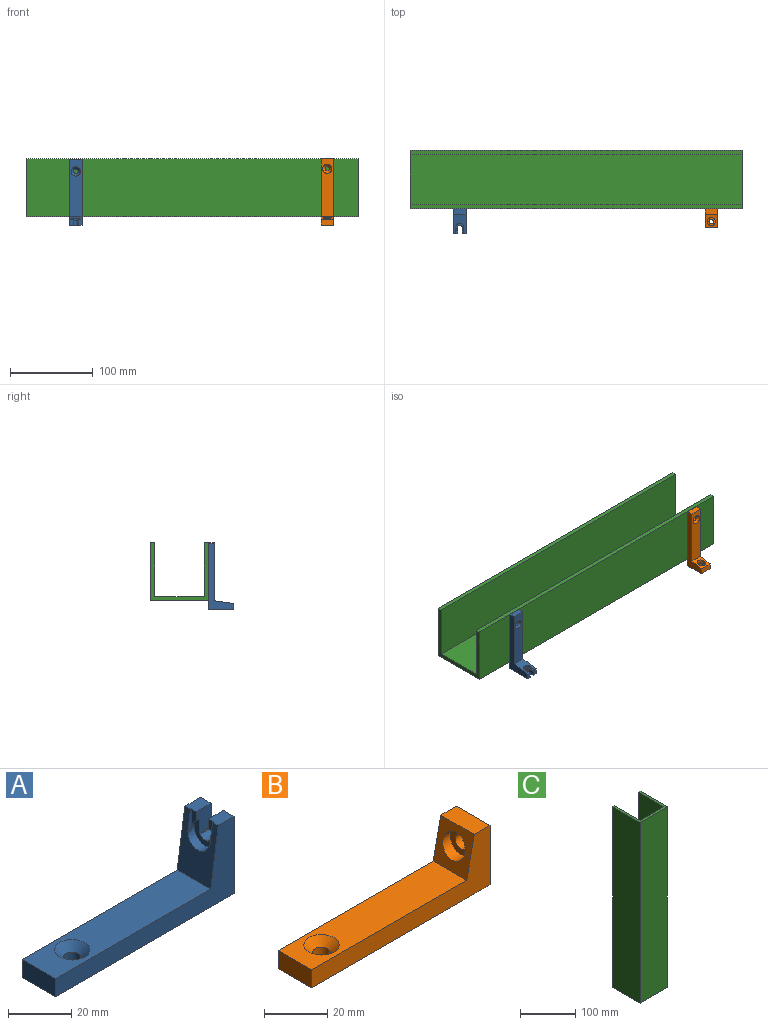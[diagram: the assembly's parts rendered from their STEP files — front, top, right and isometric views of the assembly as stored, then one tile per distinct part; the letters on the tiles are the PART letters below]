
ASSEMBLY  parts=3 mates=2
PART A: 24 faces, bbox 80x15x30 mm
  f0: cylinder r=4.88mm len=9.75mm, axis (-1,0,0), area 58.8mm2, adj f1,f2,f3,f7,f18,f19,f22,f23
  f1: plane 23x15mm, normal (-0.99,0,0.14), area 235.8mm2, adj f0,f4,f8,f9,f11,f15,f19,f20
  f2: plane 9x6.64mm, normal (0,-1,0), area 53mm2, adj f0,f5,f7,f15,f17,f23
  f3: plane 9x6.64mm, normal (0,1,0), area 53mm2, adj f0,f4,f5,f7,f16,f18
  f4: plane 7.07x4.75mm, normal (0,0,1), area 32.6mm2, adj f1,f3,f5,f11,f18,f20
  f5: plane 30x15mm, normal (1,0,0), area 396.4mm2, adj f2,f3,f4,f6,f9,f11,f12,f15
  f6: cylinder r=2.75mm len=5.42mm, axis (-1,0,0), area 29.6mm2, adj f5,f7,f16,f17
  f7: plane 9.75x8.9mm, normal (-1,0,0), area 37mm2, adj f0,f2,f3,f6,f16,f17
  f8: plane 69.58x15mm, normal (0,0,1), area 945.1mm2, adj f1,f9,f10,f11,f14
  f9: plane 80x30mm, normal (0,1,0), area 761.2mm2, adj f1,f5,f8,f10,f12,f15
  f10: plane 15x7mm, normal (-1,0,0), area 105mm2, adj f8,f9,f11,f12
  f11: plane 80x30mm, normal (0,-1,0), area 761.2mm2, adj f1,f4,f5,f8,f10,f12
  f12: plane 80x15mm, normal (0,0,-1), area 1176.2mm2, adj f5,f9,f10,f11,f13
  f13: cylinder r=2.75mm len=5.5mm, axis (0,0,1), area 71.7mm2, adj f12,f14
  f14: cone r=2.75mm half-angle=45deg, axis (0,0,1), area 105.7mm2, adj f8,f13
  f15: plane 7.07x4.75mm, normal (0,0,1), area 32.6mm2, adj f1,f2,f5,f9,f21,f23
  f16: plane 5.42x0.45mm, normal (0,0,1), area 2.4mm2, adj f3,f5,f6,f7
  f17: plane 5.42x0.45mm, normal (0,0,1), area 2.4mm2, adj f2,f5,f6,f7
  f18: plane 8x2.2mm, normal (-1,0,0), area 10.5mm2, adj f0,f3,f4,f19,f20
  f19: plane 1.6x0.1mm, normal (0,0,1), area 0.2mm2, adj f0,f1,f18,f20
  f20: plane 8x1.6mm, normal (0,1,0), area 8.2mm2, adj f1,f4,f18,f19
  f21: plane 8x1.6mm, normal (0,-1,0), area 8.2mm2, adj f1,f15,f22,f23
  f22: plane 1.6x0.1mm, normal (0,0,1), area 0.2mm2, adj f0,f1,f21,f23
  f23: plane 8x2.2mm, normal (-1,0,0), area 10.5mm2, adj f0,f2,f15,f21,f22
PART B: 13 faces, bbox 80.4x15.4x23.5 mm
  f0: plane 69.58x15mm, normal (0,0,1), area 945.1mm2, adj f1,f2,f3,f7,f8
  f1: plane 80x23.1mm, normal (0,1,0), area 700.9mm2, adj f0,f2,f4,f5,f8,f9
  f2: plane 15x7mm, normal (-1,0,0), area 105mm2, adj f0,f1,f3,f5
  f3: plane 80x23.1mm, normal (0,-1,0), area 700.9mm2, adj f0,f2,f4,f5,f8,f9
  f4: plane 23.1x15mm, normal (1,0,0), area 322.8mm2, adj f1,f3,f5,f9,f11
  f5: plane 80x15mm, normal (0,0,-1), area 1176.2mm2, adj f1,f2,f3,f4,f6
  f6: cylinder r=2.75mm len=5.5mm, axis (0,0,1), area 71.7mm2, adj f5,f7
  f7: cone r=2.75mm half-angle=45deg, axis (0,0,1), area 105.7mm2, adj f0,f6
  f8: plane 16.53x15.43mm, normal (-0.98,0,0.2), area 170.4mm2, adj f0,f1,f3,f9,f10
  f9: plane 15x7.07mm, normal (0,0,1), area 106.1mm2, adj f1,f3,f4,f8
  f10: cylinder r=4.88mm len=9.75mm, axis (-1,0,0), area 97.3mm2, adj f8,f12
  f11: cylinder r=2.75mm len=5.5mm, axis (-1,0,0), area 93.7mm2, adj f4,f12
  f12: plane 9.75x9.75mm, normal (-1,0,0), area 50.9mm2, adj f10,f11
PART C: 10 faces, bbox 70x70x400 mm
  f0: plane 400x5mm, normal (0,1,0), area 2000mm2, adj f1,f7,f8,f9
  f1: plane 400x70mm, normal (-1,0,0), area 28000mm2, adj f0,f2,f8,f9
  f2: plane 400x70mm, normal (0,-1,0), area 28000mm2, adj f1,f3,f8,f9
  f3: plane 400x70mm, normal (1,0,0), area 28000mm2, adj f2,f4,f8,f9
  f4: plane 400x5mm, normal (0,1,0), area 2000mm2, adj f3,f5,f8,f9
  f5: plane 400x65mm, normal (-1,0,0), area 26000mm2, adj f4,f6,f8,f9
  f6: plane 400x60mm, normal (0,1,0), area 24000mm2, adj f5,f7,f8,f9
  f7: plane 400x65mm, normal (1,0,0), area 26000mm2, adj f0,f6,f8,f9
  f8: plane 70x70mm, normal (0,0,1), area 1000mm2, adj f0,f1,f2,f3,f4,f5,f6,f7
  f9: plane 70x70mm, normal (0,0,-1), area 1000mm2, adj f0,f1,f2,f3,f4,f5,f6,f7
PLACE A rot(axis=(0.58,0.58,-0.58),120deg) t=(-212.25,48.76,30.61)mm
PLACE B rot(axis=(0.58,0.58,-0.58),120deg) t=(90.71,48.76,30.71)mm
PLACE C rot(axis=(0.58,-0.58,-0.58),120deg) t=(127.75,98.75,17.79)mm
MATE planar B.f5 <-> C.f3  axis (0,1,0) through (90.71,48.76,30.14)mm
MATE planar A.f12 <-> C.f3  axis (0,1,0) through (-212.25,48.76,30.1)mm
